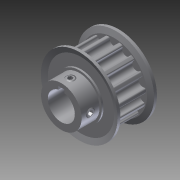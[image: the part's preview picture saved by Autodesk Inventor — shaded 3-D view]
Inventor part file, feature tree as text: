
AUTODESK INVENTOR PART (.ipt)
format: ipt  version: 2012 (Build 160160000, 160)  size: 319,488 bytes
history: native  units: in
note: dims shown in document units (in); Inventor stores cm internally (conversion verified against a paired STEP export)
features: extrude x1, imported_body x1, sketch x1
ambient origin geometry x8: Origin, YZ Plane, XZ Plane, XY Plane, X Axis, Y Axis, Z Axis, Center Point
feature tree (3):
  extrude  "Extrusion1"  Depth=0.0394in
  imported_body  "Base1"
  sketch  "Sketch1"  dims[d0=0.375in d1=0.0394in d4=0.0394in d5=0.1481in d6=0.0787in d7=0.0787in d8=0.3937in d9=0.0in]
